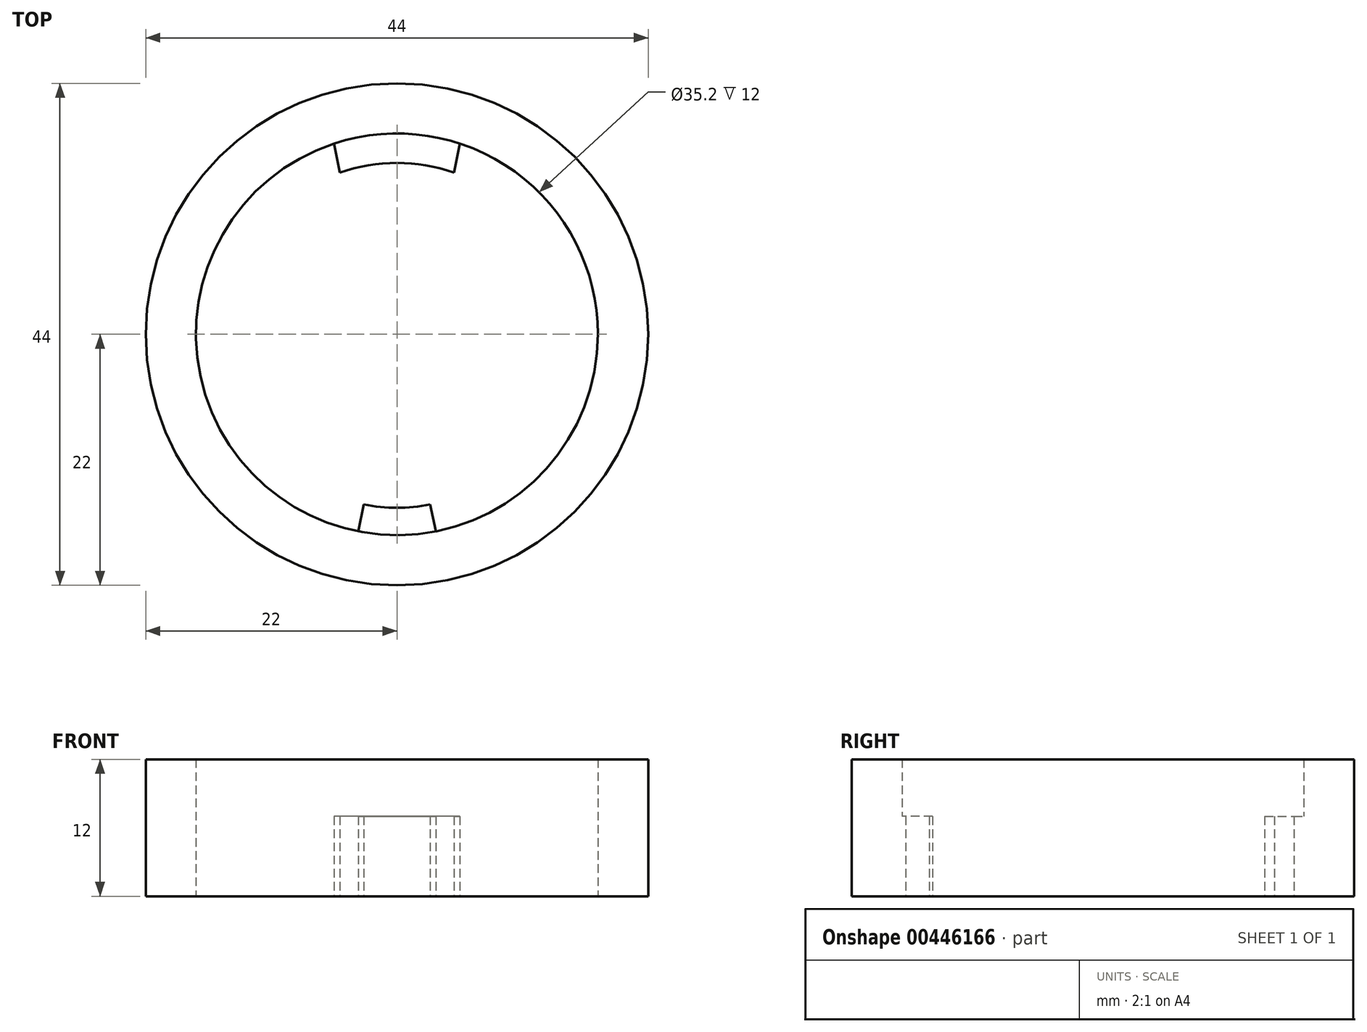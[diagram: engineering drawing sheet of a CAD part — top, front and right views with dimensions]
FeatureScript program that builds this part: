
annotation { "Feature Type Name" : "Feature", "Feature Type Description" : "" }
export const myFeature = defineFeature(function(context is Context, id is Id, definition is map)
    precondition{}
    {
        {
            var Q0;
            Q0=qCreatedBy(makeId("Top.planeOp"),FACE);
            var sketch = newSketch(context, id + "F0", { "sketchPlane" : qUnion([Q0])});
            skCircle(sketch, "E0", {"center": v(0, 0) * mm, "radius": 8.5 * mm});
            skCircle(sketch, "E1", {"center": v(0, 0) * mm, "radius": 9.5 * mm});
            skCircle(sketch, "E2", {"center": v(0, 0) * mm, "radius": 17.6 * mm});
            skCircle(sketch, "E3", {"center": v(0, 0) * mm, "radius": 22 * mm});
            skPoint(sketch, "E4", {"position": v(-3.4, -17.27) * mm});
            skPoint(sketch, "E5", {"position": v(3.4, -17.27) * mm});
            skLineSegment(sketch, "E6", {"start": v(-2.9, -14.92) * mm, "end": v(-3.4, -17.27) * mm});
            skLineSegment(sketch, "E7", {"start": v(2.9, -14.92) * mm, "end": v(3.4, -17.27) * mm});
            skPoint(sketch, "E8", {"position": v(-5.5, 16.72) * mm});
            skPoint(sketch, "E9", {"position": v(5.5, 16.72) * mm});
            skLineSegment(sketch, "E10", {"start": v(-5, 14.17) * mm, "end": v(-5.5, 16.72) * mm});
            skLineSegment(sketch, "E11", {"start": v(5, 14.17) * mm, "end": v(5.5, 16.72) * mm});
            skArc(sketch, "E12", {"start": v(-2.9, -14.92) * mm, "mid": v(0, -15.2) * mm, "end": v(2.9, -14.92) * mm});
            skArc(sketch, "E13", {"start": v(-5, 14.17) * mm, "mid": v(0, 15.02) * mm, "end": v(5, 14.17) * mm});
            skSolve(sketch);
        }
        {
            var Q0;
            Q0=makeQuery(id+"F0.imprint","IMPRINT",FACE,{"disambiguationData":[TD([[makeQuery(id+"F0.imprint","IMPRINT",EDGE,{"derivedFrom":sQuery(id+"F0.wireOp",EDGE,"E3")}),1.0]])]});
            extrude(context, id + "F1", {"entities" : qUnion([Q0]), "depth" : 12 * mm});
        }
        {
            var Q0;
            {var subQ0=sQuery(id+"F0.wireOp",EDGE,"E10");Q0=makeQuery(id+"F0.imprint","IMPRINT",FACE,{"disambiguationData":[TD([[makeQuery(id+"F0.imprint","IMPRINT",EDGE,{"derivedFrom":subQ0}),-1.0]])]});}
            var Q1;
            {var subQ0=sQuery(id+"F0.wireOp",EDGE,"E6");Q1=makeQuery(id+"F0.imprint","IMPRINT",FACE,{"disambiguationData":[TD([[makeQuery(id+"F0.imprint","IMPRINT",EDGE,{"derivedFrom":subQ0}),1.0]])]});}
            extrude(context, id + "F2", {"entities" : qUnion([Q0, Q1]), "operationType" : NewBodyOperationType.ADD, "depth" : 7 * mm});
        }
    });
